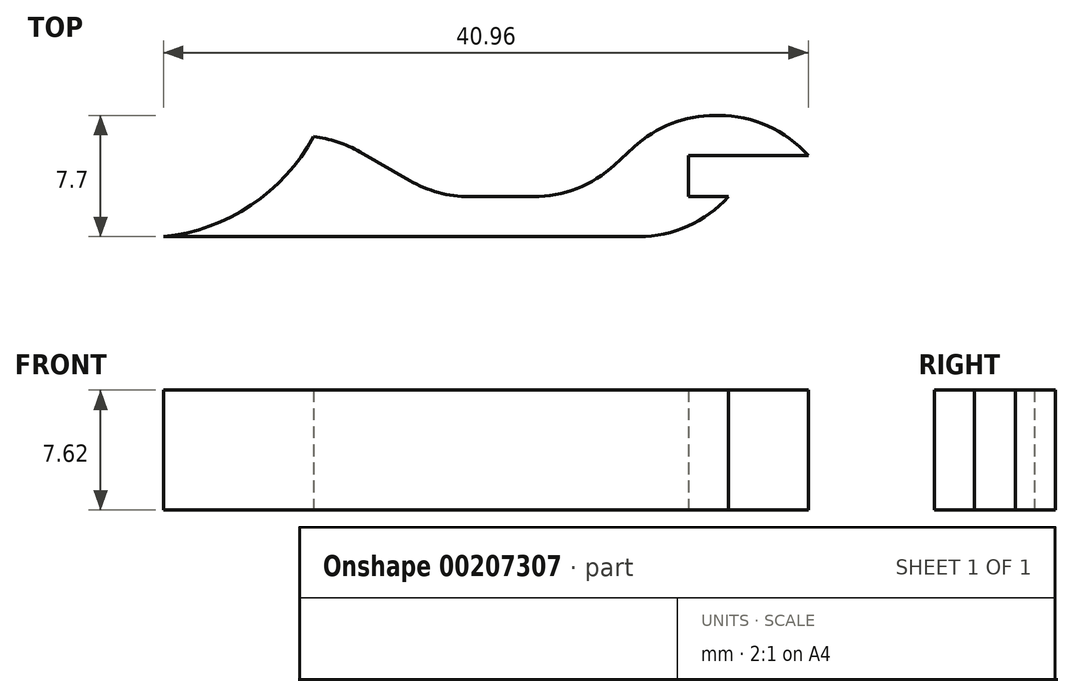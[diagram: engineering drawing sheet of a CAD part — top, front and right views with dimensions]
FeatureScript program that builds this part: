
annotation { "Feature Type Name" : "Feature", "Feature Type Description" : "" }
export const myFeature = defineFeature(function(context is Context, id is Id, definition is map)
    precondition{}
    {
        {
            var Q0;
            Q0=qCreatedBy(makeId("Top.planeOp"),FACE);
            var sketch = newSketch(context, id + "F0", { "sketchPlane" : qUnion([Q0])});
            skLineSegment(sketch, "E0", {"start": v(0, 0) * mm, "end": v(23.81, 0) * mm});
            skLineSegment(sketch, "E1", {"start": v(23.81, 0) * mm, "end": v(26.35, 0) * mm});
            skLineSegment(sketch, "E2", {"start": v(26.35, 0) * mm, "end": v(26.35, 2.54) * mm});
            skLineSegment(sketch, "E3", {"start": v(26.35, 2.54) * mm, "end": v(23.81, 2.54) * mm});
            skLineSegment(sketch, "E4", {"start": v(23.81, 2.54) * mm, "end": v(23.81, 5.16) * mm});
            skLineSegment(sketch, "E5", {"start": v(23.81, 5.16) * mm, "end": v(31.43, 5.16) * mm});
            skLineSegment(sketch, "E6", {"start": v(31.43, 5.16) * mm, "end": v(31.43, 7.7) * mm});
            skLineSegment(sketch, "E7", {"start": v(31.43, 7.7) * mm, "end": v(22.54, 7.7) * mm});
            skLineSegment(sketch, "E8", {"start": v(22.54, 7.7) * mm, "end": v(16.93, 2.54) * mm});
            skLineSegment(sketch, "E9", {"start": v(16.93, 2.54) * mm, "end": v(7.87, 2.54) * mm});
            skLineSegment(sketch, "E10", {"start": v(7.87, 2.54) * mm, "end": v(1.27, 6.35) * mm});
            skLineSegment(sketch, "E11", {"start": v(1.27, 6.35) * mm, "end": v(0, 6.35) * mm});
            skLineSegment(sketch, "E12", {"start": v(0, 0) * mm, "end": v(-9.53, 0) * mm});
            skArc(sketch, "E13", {"start": v(-9.53, 0) * mm, "mid": v(-3.97, 2) * mm, "end": v(0, 6.35) * mm});
            skPoint(sketch, "E13.third.point", {"position": v(-12.64, 24.26) * mm});
            skSolve(sketch);
        }
        {
            var Q0;
            Q0 = qSketchRegion(id + "F0", true);
            extrude(context, id + "F1", {"entities" : qUnion([Q0]), "depth" : 7.62 * mm});
        }
        {
            var Q0;
            Q0=makeQuery(id+"F1.opExtrude","SWEPT_EDGE",EDGE,{"disambiguationData":[OSD([sQuery(id+"F0.wireOp",EDGE,"E10"),sQuery(id+"F0.wireOp",EDGE,"E11")])]});
            var Q1;
            Q1=makeQuery(id+"F1.opExtrude","SWEPT_EDGE",EDGE,{"disambiguationData":[OSD([sQuery(id+"F0.wireOp",EDGE,"E9"),sQuery(id+"F0.wireOp",EDGE,"E10")])]});
            var Q2;
            Q2=makeQuery(id+"F1.opExtrude","SWEPT_EDGE",EDGE,{"disambiguationData":[OSD([sQuery(id+"F0.wireOp",EDGE,"E8"),sQuery(id+"F0.wireOp",EDGE,"E9")])]});
            var Q3;
            Q3=makeQuery(id+"F1.opExtrude","SWEPT_EDGE",EDGE,{"disambiguationData":[OSD([sQuery(id+"F0.wireOp",EDGE,"E7"),sQuery(id+"F0.wireOp",EDGE,"E8")])]});
            fillet(context, id + "F2", {"entities" : qUnion([Q0, Q1, Q2, Q3]), "radius" : 7.62 * mm, "tangentPropagation" : true, "allowEdgeOverflow" : false});
        }
        {
            var Q0;
            Q0=makeQuery(id+"F1.opExtrude","SWEPT_EDGE",EDGE,{"disambiguationData":[OSD([sQuery(id+"F0.wireOp",EDGE,"E6"),sQuery(id+"F0.wireOp",EDGE,"E7")])]});
            var Q1;
            Q1=makeQuery(id+"F1.opExtrude","SWEPT_EDGE",EDGE,{"disambiguationData":[OSD([sQuery(id+"F0.wireOp",EDGE,"E1"),sQuery(id+"F0.wireOp",EDGE,"E2")])]});
            fillet(context, id + "F3", {"entities" : qUnion([Q0, Q1]), "radius" : 7.62 * mm, "tangentPropagation" : true, "allowEdgeOverflow" : false});
        }
    });
